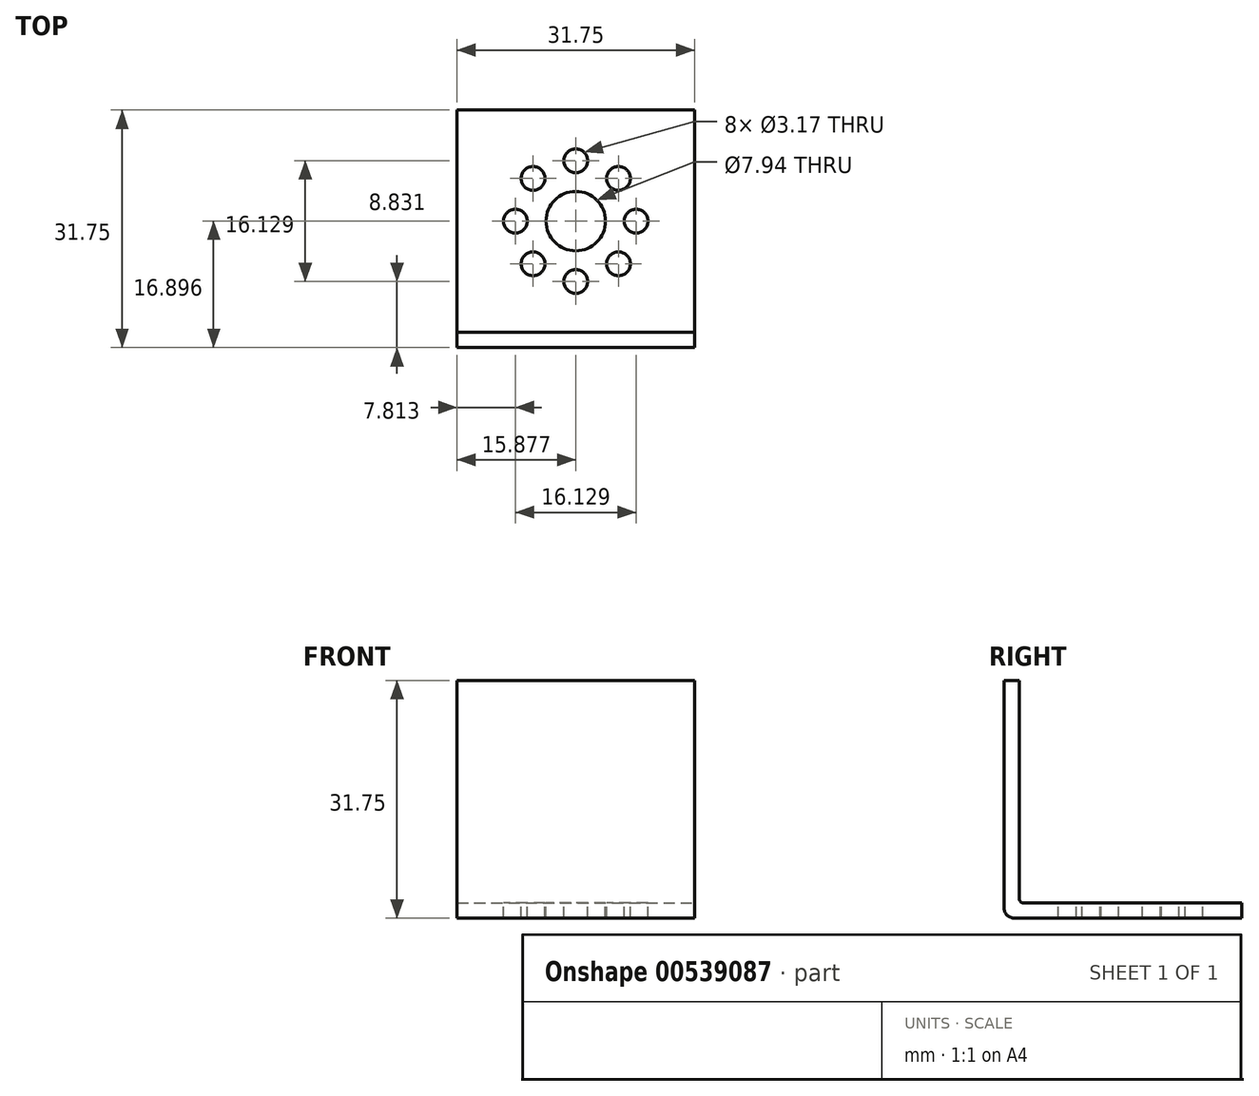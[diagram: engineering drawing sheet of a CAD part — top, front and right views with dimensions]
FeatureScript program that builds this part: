
annotation { "Feature Type Name" : "Feature", "Feature Type Description" : "" }
export const myFeature = defineFeature(function(context is Context, id is Id, definition is map)
    precondition{}
    {
        {
            var Q0;
            Q0=qCreatedBy(makeId("Top.planeOp"),FACE);
            var sketch = newSketch(context, id + "F0", { "sketchPlane" : qUnion([Q0])});
            skLineSegment(sketch, "E0.bottom", {"start": v(-30.22, -34.04) * mm, "end": v(1.53, -34.04) * mm});
            skLineSegment(sketch, "E0.top", {"start": v(-30.22, -2.29) * mm, "end": v(1.53, -2.29) * mm});
            skLineSegment(sketch, "E0.left", {"start": v(-30.22, -34.04) * mm, "end": v(-30.22, -2.29) * mm});
            skLineSegment(sketch, "E0.right", {"start": v(1.53, -34.04) * mm, "end": v(1.53, -2.29) * mm});
            skSolve(sketch);
        }
        {
            var Q0;
            Q0 = qSketchRegion(id + "F0", true);
            extrude(context, id + "F1", {"entities" : qUnion([Q0]), "depth" : 2.03 * mm, "offsetDistance" : 25.4 * mm});
        }
        {
            var Q0;
            Q0=makeQuery(id+"F1.opExtrude","SWEPT_FACE",FACE,{"disambiguationData":[OSD([sQuery(id+"F0.wireOp",EDGE,"E0.bottom")])]});
            var sketch = newSketch(context, id + "F2", { "sketchPlane" : qUnion([Q0])});
            skLineSegment(sketch, "E1.bottom", {"start": v(-30.22, 0) * mm, "end": v(1.53, 0) * mm});
            skLineSegment(sketch, "E1.top", {"start": v(-30.22, 31.75) * mm, "end": v(1.53, 31.75) * mm});
            skLineSegment(sketch, "E1.left", {"start": v(-30.22, 0) * mm, "end": v(-30.22, 31.75) * mm});
            skLineSegment(sketch, "E1.right", {"start": v(1.53, 0) * mm, "end": v(1.53, 31.75) * mm});
            skSolve(sketch);
        }
        {
            var Q0;
            Q0 = qSketchRegion(id + "F2", true);
            extrude(context, id + "F3", {"entities" : qUnion([Q0]), "operationType" : NewBodyOperationType.ADD, "oppositeDirection" : true, "depth" : 2.03 * mm, "offsetDistance" : 25.4 * mm});
        }
        {
            var Q0;
            Q0=makeQuery(id+"F3.boolean.opBoolean","INTERSECT",EDGE,{"derivedFrom":[makeQuery(id+"F1.opExtrude","CAP_FACE",FACE,{"disambiguationData":[OSD([sQuery(id+"F0.wireOp",EDGE,"E0.bottom"),sQuery(id+"F0.wireOp",EDGE,"E0.top"),sQuery(id+"F0.wireOp",EDGE,"E0.left"),sQuery(id+"F0.wireOp",EDGE,"E0.right")])],"isStart":false}),makeQuery(id+"F3.opExtrude","CAP_FACE",FACE,{"disambiguationData":[OSD([sQuery(id+"F2.wireOp",EDGE,"E1.bottom"),sQuery(id+"F2.wireOp",EDGE,"E1.top"),sQuery(id+"F2.wireOp",EDGE,"E1.left"),sQuery(id+"F2.wireOp",EDGE,"E1.right")])],"isStart":false})]});
            fillet(context, id + "F4", {"entities" : qUnion([Q0]), "radius" : 0.5 * mm, "tangentPropagation" : true, "allowEdgeOverflow" : false});
        }
        {
            var Q0;
            Q0=makeQuery(id+"F1.opExtrude","CAP_EDGE",EDGE,{"disambiguationData":[OSD([sQuery(id+"F0.wireOp",EDGE,"E0.bottom")])],"isStart":true});
            fillet(context, id + "F5", {"entities" : qUnion([Q0]), "radius" : 1.27 * mm, "tangentPropagation" : true, "allowEdgeOverflow" : false});
        }
        {
            var Q0;
            Q0=makeQuery(id+"F1.opExtrude","CAP_FACE",FACE,{"disambiguationData":[OSD([sQuery(id+"F0.wireOp",EDGE,"E0.bottom"),sQuery(id+"F0.wireOp",EDGE,"E0.top"),sQuery(id+"F0.wireOp",EDGE,"E0.left"),sQuery(id+"F0.wireOp",EDGE,"E0.right")])],"isStart":false});
            var sketch = newSketch(context, id + "F6", { "sketchPlane" : qUnion([Q0])});
            skCircle(sketch, "E2.0", {"center": v(-14.34, -9.08) * mm, "radius": 1.59 * mm});
            skCircle(sketch, "E3.0", {"center": v(-20.05, -11.44) * mm, "radius": 1.59 * mm});
            skCircle(sketch, "E4.0", {"center": v(-22.4, -17.14) * mm, "radius": 1.59 * mm});
            skCircle(sketch, "E5.0", {"center": v(-20.05, -22.85) * mm, "radius": 1.59 * mm});
            skCircle(sketch, "E6.0", {"center": v(-14.34, -25.2) * mm, "radius": 1.59 * mm});
            skCircle(sketch, "E7.0", {"center": v(-8.64, -22.85) * mm, "radius": 1.59 * mm});
            skCircle(sketch, "E8.0", {"center": v(-6.28, -17.14) * mm, "radius": 1.59 * mm});
            skCircle(sketch, "E9.0", {"center": v(-8.64, -11.44) * mm, "radius": 1.59 * mm});
            skCircle(sketch, "E10.0", {"center": v(-14.34, -17.14) * mm, "radius": 3.97 * mm});
            skSolve(sketch);
        }
        {
            var Q0;
            Q0 = qSketchRegion(id + "F6", true);
            extrude(context, id + "F7", {"entities" : qUnion([Q0]), "operationType" : NewBodyOperationType.REMOVE, "oppositeDirection" : true, "depth" : 25.4 * mm, "offsetDistance" : 25.4 * mm});
        }
    });
